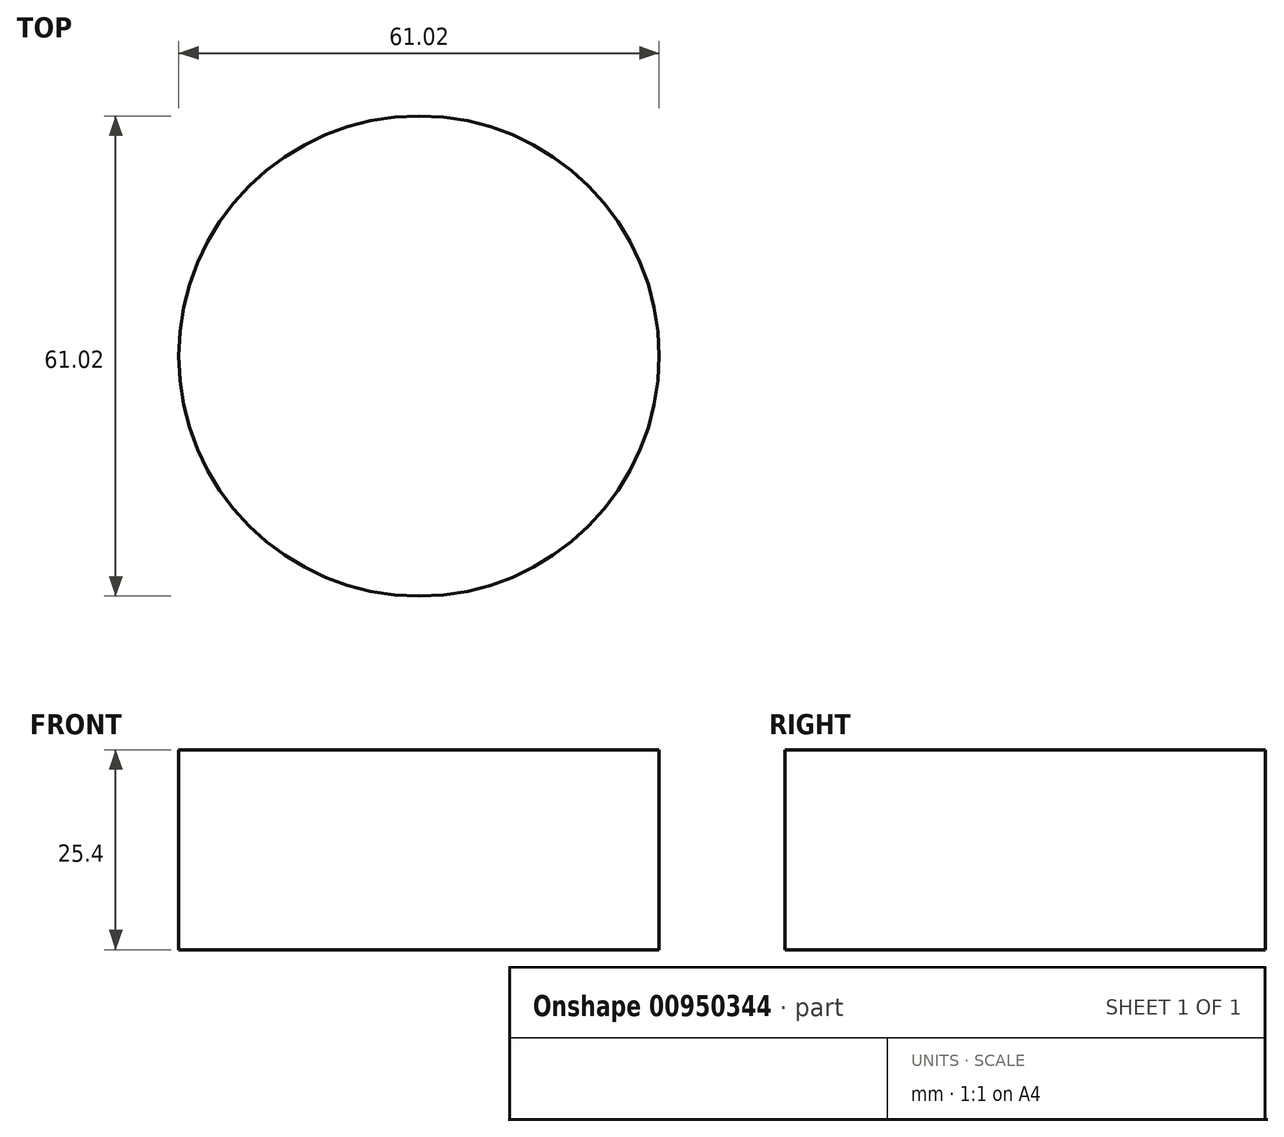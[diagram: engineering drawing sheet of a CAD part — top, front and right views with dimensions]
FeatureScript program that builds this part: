
annotation { "Feature Type Name" : "Feature", "Feature Type Description" : "" }
export const myFeature = defineFeature(function(context is Context, id is Id, definition is map)
    precondition{}
    {
        {
            var Q0;
            Q0=qCreatedBy(makeId("Top.planeOp"),FACE);
            var sketch = newSketch(context, id + "F0", { "sketchPlane" : qUnion([Q0])});
            skCircle(sketch, "E0", {"center": v(0, 0) * mm, "radius": 30.5 * mm});
            skSolve(sketch);
        }
        {
            var Q0;
            Q0=makeQuery(id+"F0.imprint","IMPRINT",FACE,{"disambiguationData":[TD([[makeQuery(id+"F0.imprint","IMPRINT",EDGE,{"derivedFrom":sQuery(id+"F0.wireOp",EDGE,"E0")}),1.0]])]});
            extrude(context, id + "F1", {"entities" : qUnion([Q0]), "depth" : 25.4 * mm, "offsetDistance" : 25.4 * mm});
        }
    });
